# Revit family: Legrand_Single_phase_transformers
name_source: partatom
category: Installations électriques
revit_build: Autodesk Revit 2018 (Build: 20170223_1515(x64)
units: mm (PartAtom-declared; Revit-internal decimal feet)

## family parameters
Basée sur le plan de construction = Non
Conserver l'orientation des annotations = Non
Cote de connecteur circulaire = Utiliser le diamètre
Couper avec des vides une fois chargée = Non
Numéro OmniClass = 23.80.00.00
Partagée = Non
Point de calcul de pièce = Non
Titre OmniClass = Electric Power and Lighting
Toujours verticalement = Oui
Type d'élément = Normal

## types (4) — shared parameters
Characteristic = Class I - IP21 - IK08
Fabricant = Legrand
General Conditions of Use = https://export.legrand.com
Insulating = class H
Modèle = Single phase autotransformer
Operating voltage = 400-230 V or 230-400 V by reversibility compensated up to 16kVA
URL = www.legrand.com

## per-type parameters (varying)
| type | 042265, 042266 | 042267 | 042268 | Primary Cable Section | Secondary cable section | Ucc (%) | dimension A | dimension B | dimension C | empty loss | fixing F | fixing G | fixing diameter | max totaly loss | power | weight |
| single phase transformer 042265 | Oui | Non | Non | 10mm² | 10 mm² | 1.7 | 250 mm  [stored 0.82021 ft] | 270 mm  [stored 0.885827 ft] | 253 mm  [stored 0.830052 ft] | 55 W | 230 mm  [stored 0.754593 ft] | 91 mm  [stored 0.298556 ft] | 7 mm  [stored 0.0229659 ft] | 105 W | 3 kVA | 21.00 kg |
| single phase transformer 042267 | Non | Oui | Non | 35mm² | 35 mm² | 1.1 | 320 mm  [stored 1.04987 ft] | 330 mm | 253 mm  [stored 0.830052 ft] | 77 W | 300 mm | 101 mm  [stored 0.331365 ft] | 9 mm  [stored 0.0295276 ft] | 136 W | 6 kVA | 38.00 kg |
| single phase transformer 042268 | Non | Non | Oui | 16mm² | 16 mm² | 1.3 | 300 mm | 390 mm  [stored 1.27953 ft] | 230 mm  [stored 0.754593 ft] | 83 W | 280 mm  [stored 0.918635 ft] | 130 mm  [stored 0.426509 ft] | 9 mm  [stored 0.0295276 ft] | 189 W | 8 kVA | 37.20 kg |
| single phase transformer 042266 | Oui | Non | Non | 16mm² | 16 mm² | 1.1 | 250 mm  [stored 0.82021 ft] | 270 mm  [stored 0.885827 ft] | 253 mm  [stored 0.830052 ft] | 66 W | 230 mm  [stored 0.754593 ft] | 130 mm  [stored 0.426509 ft] | 7 mm  [stored 0.0229659 ft] | 106 W | 4 kVA | 28.00 kg |

note: [stored X ft] marks values corroborated as IEEE doubles in the binary element streams (Revit-internal decimal feet)
